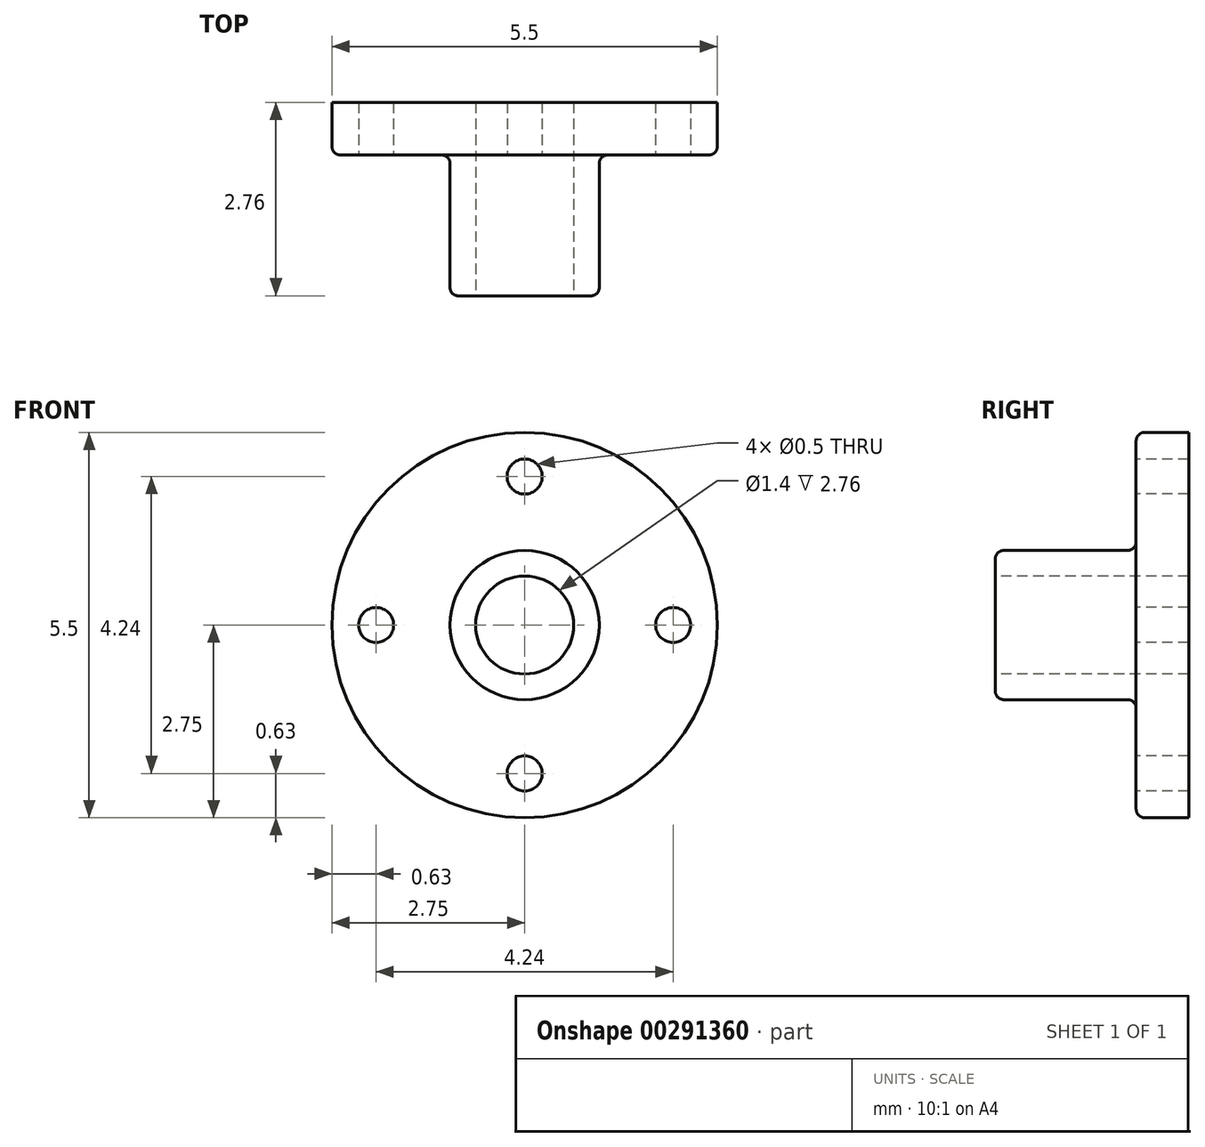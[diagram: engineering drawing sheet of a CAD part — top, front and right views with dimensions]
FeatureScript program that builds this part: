
annotation { "Feature Type Name" : "Feature", "Feature Type Description" : "" }
export const myFeature = defineFeature(function(context is Context, id is Id, definition is map)
    precondition{}
    {
        {
            var Q0;
            Q0=qCreatedBy(makeId("Top.planeOp"),FACE);
            var sketch = newSketch(context, id + "F0", { "sketchPlane" : qUnion([Q0])});
            skLineSegment(sketch, "E0.bottom", {"start": v(0, 0) * mm, "end": v(1.06, 0) * mm});
            skLineSegment(sketch, "E0.top", {"start": v(0, 2.76) * mm, "end": v(2.75, 2.76) * mm});
            skLineSegment(sketch, "E0.left", {"start": v(0, 0) * mm, "end": v(0, 2.76) * mm});
            skLineSegment(sketch, "E0.right", {"start": v(2.75, 2) * mm, "end": v(2.75, 2.76) * mm});
            skPoint(sketch, "E1", {"position": v(2.75, 2) * mm});
            skPoint(sketch, "E2", {"position": v(1.06, 0) * mm});
            skPoint(sketch, "E3", {"position": v(1.06, 2) * mm});
            skLineSegment(sketch, "E4.top", {"start": v(1.06, 2) * mm, "end": v(2.75, 2) * mm});
            skLineSegment(sketch, "E4.left", {"start": v(1.06, 0) * mm, "end": v(1.06, 2) * mm});
            skSolve(sketch);
        }
        {
            var Q0;
            Q0=makeQuery(id+"F0.imprint","IMPRINT",FACE,{"disambiguationData":[TD([[makeQuery(id+"F0.imprint","IMPRINT",EDGE,{"derivedFrom":sQuery(id+"F0.wireOp",EDGE,"E0.bottom")}),1.0]])]});
            var Q1;
            Q1=sQuery(id+"F0.wireOp",EDGE,"E0.left");
            revolve(context, id + "F1", {"entities" : qUnion([Q0]), "axis" : qUnion([Q1]), "revolveType" : RevolveType.FULL});
        }
        {
            var Q0;
            Q0=makeQuery(id+"F1.opRevolve","SWEPT_FACE",FACE,{"disambiguationData":[OSD([sQuery(id+"F0.wireOp",EDGE,"E0.bottom")])]});
            var sketch = newSketch(context, id + "F2", { "sketchPlane" : qUnion([Q0])});
            skCircle(sketch, "E5", {"center": v(0, 0) * mm, "radius": 0.7 * mm});
            skSolve(sketch);
        }
        {
            var Q0;
            Q0 = qSketchRegion(id + "F2", true);
            extrude(context, id + "F3", {"entities" : qUnion([Q0]), "operationType" : NewBodyOperationType.REMOVE, "endBound" : BoundingType.THROUGH_ALL, "oppositeDirection" : true, "depth" : 25 * mm});
        }
        {
            var Q0;
            Q0=makeQuery(id+"F1.opRevolve","SWEPT_FACE",FACE,{"disambiguationData":[OSD([sQuery(id+"F0.wireOp",EDGE,"E4.top")])]});
            var sketch = newSketch(context, id + "F4", { "sketchPlane" : qUnion([Q0])});
            skCircle(sketch, "E6", {"center": v(0, 2.12) * mm, "radius": 0.25 * mm});
            skCircle(sketch, "E7", {"center": v(2.12, 0) * mm, "radius": 0.25 * mm});
            skCircle(sketch, "E8", {"center": v(0, -2.12) * mm, "radius": 0.25 * mm});
            skCircle(sketch, "E9", {"center": v(-2.12, 0) * mm, "radius": 0.25 * mm});
            skSolve(sketch);
        }
        {
            var Q0;
            Q0 = qSketchRegion(id + "F4", true);
            extrude(context, id + "F5", {"entities" : qUnion([Q0]), "operationType" : NewBodyOperationType.REMOVE, "endBound" : BoundingType.THROUGH_ALL, "oppositeDirection" : true, "depth" : 25 * mm});
        }
        {
            var Q0;
            Q0=makeQuery(id+"F1.opRevolve","SWEPT_EDGE",EDGE,{"disambiguationData":[OSD([sQuery(id+"F0.wireOp",EDGE,"E0.right"),sQuery(id+"F0.wireOp",EDGE,"E4.top")])]});
            var Q1;
            Q1=makeQuery(id+"F1.opRevolve","SWEPT_EDGE",EDGE,{"disambiguationData":[OSD([sQuery(id+"F0.wireOp",EDGE,"E4.top"),sQuery(id+"F0.wireOp",EDGE,"E4.left")])]});
            var Q2;
            Q2=makeQuery(id+"F1.opRevolve","SWEPT_EDGE",EDGE,{"disambiguationData":[OSD([sQuery(id+"F0.wireOp",EDGE,"E0.bottom"),sQuery(id+"F0.wireOp",EDGE,"E4.left")])]});
            fillet(context, id + "F6", {"entities" : qUnion([Q0, Q1, Q2]), "radius" : .12 * mm, "tangentPropagation" : true, "allowEdgeOverflow" : false});
        }
    });
